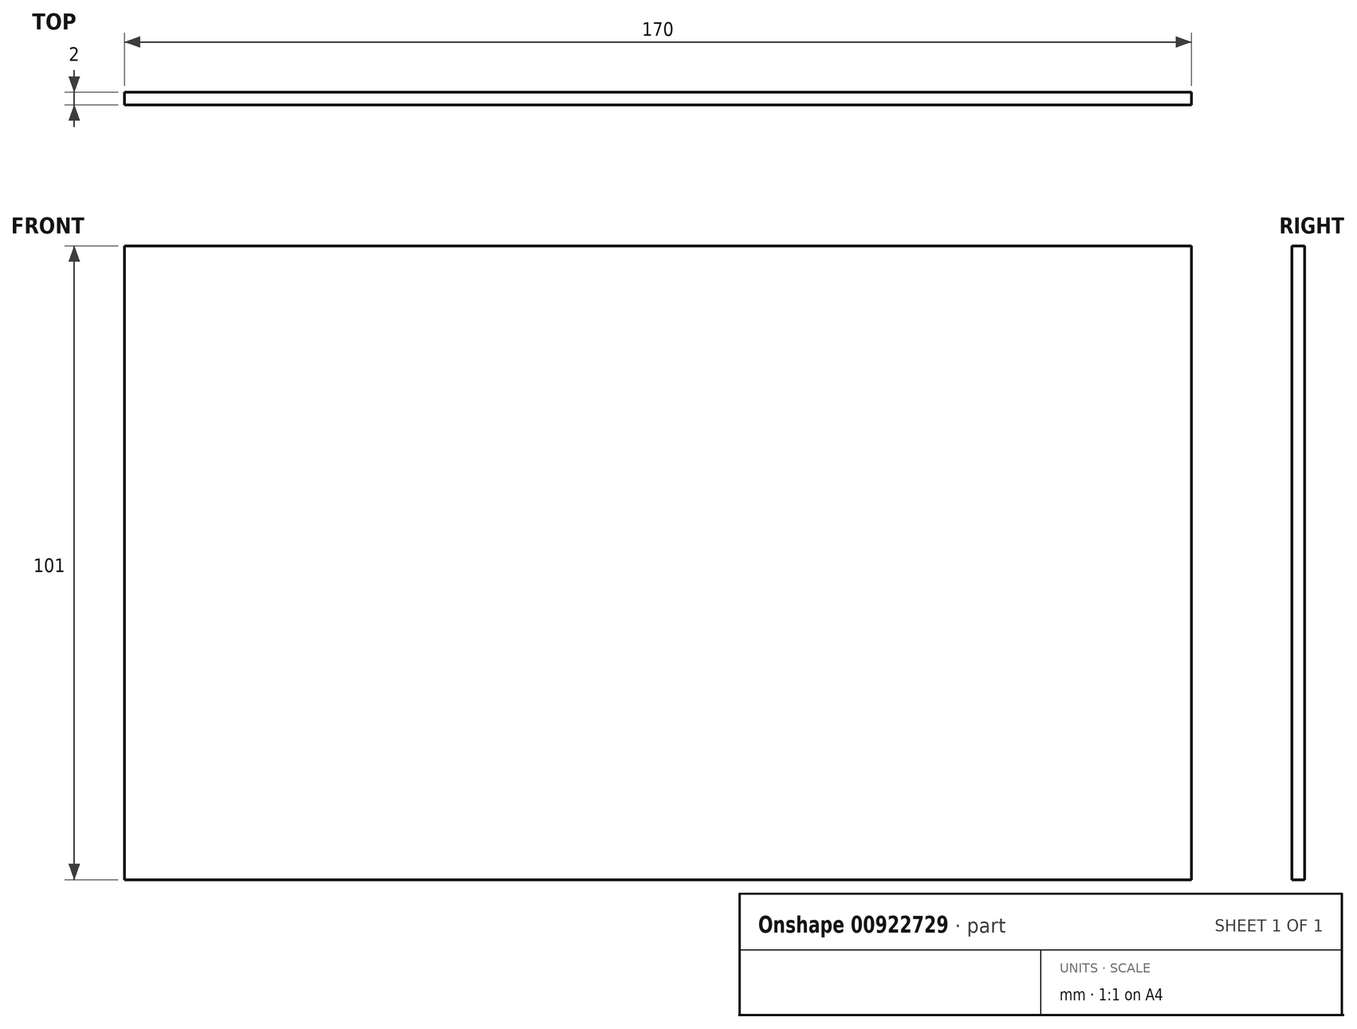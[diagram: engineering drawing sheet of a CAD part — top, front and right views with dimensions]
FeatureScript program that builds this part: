
annotation { "Feature Type Name" : "Feature", "Feature Type Description" : "" }
export const myFeature = defineFeature(function(context is Context, id is Id, definition is map)
    precondition{}
    {
        {
            var Q0;
            Q0=qCreatedBy(makeId("Front.planeOp"),FACE);
            var sketch = newSketch(context, id + "F0", { "sketchPlane" : qUnion([Q0])});
            skLineSegment(sketch, "E0.bottom", {"start": v(85, -50.5) * mm, "end": v(-85, -50.5) * mm});
            skLineSegment(sketch, "E0.top", {"start": v(85, 50.5) * mm, "end": v(-85, 50.5) * mm});
            skLineSegment(sketch, "E0.left", {"start": v(85, -50.5) * mm, "end": v(85, 50.5) * mm});
            skLineSegment(sketch, "E0.right", {"start": v(-85, -50.5) * mm, "end": v(-85, 50.5) * mm});
            skPoint(sketch, "E0.middle", {"position": v(0, 0) * mm});
            skSolve(sketch);
        }
        {
            var Q0;
            Q0 = qSketchRegion(id + "F0", true);
            extrude(context, id + "F1", {"entities" : qUnion([Q0]), "endBound" : BoundingType.SYMMETRIC, "depth" : 2 * mm, "offsetDistance" : 25 * mm});
        }
    });
